# Revit family: J2 PET Felt Geo Panelsl
name_source: partatom
category: Generic Models
units: mm (PartAtom-declared; Revit-internal decimal feet)

## family parameters
Can host rebar = No
Cut with Voids When Loaded = No
Host = Face
Maintain Annotation Orientation = No
Part Type = Normal
Room Calculation Point = No
Round Connector Dimension = Use Diameter
Shared = No

## types (12) — shared parameters
Beveled Edges = Yes
Default Elevation = 0' - 0"
Felt color = <By Category>
Manufacturer = J2 Systems
Product Line = Geo Panel
Release Date = 2020
URL = https://www.j2systems.net

## per-type parameters (varying)
| type | Length | Thickness | Width |
| Geo Panel 1.5"x9"x9" | 0' - 9" | 0' - 1 1/2" | 0' - 9" |
| Geo Panel 1.5"x18"x18" | 1' - 6" | 0' - 1 1/2" | 1' - 6" |
| Geo Panel 1.5"x36"x36" | 3' - 0" | 0' - 1 1/2" | 3' - 0" |
| Geo Panel 1.5"x36"x18" | 3' - 0" | 0' - 1 1/2" | 1' - 6" |
| Geo Panel 1.5"x36"x9" | 3' - 0" | 0' - 1 1/2" | 0' - 9" |
| Geo Panel 1.5"x18"x9" | 1' - 6" | 0' - 1 1/2" | 0' - 9" |
| Geo Panel 2"x9"x9" | 0' - 9" | 0' - 2" | 0' - 9" |
| Geo Panel 2"x18"x18" | 1' - 6" | 0' - 2" | 1' - 6" |
| Geo Panel 2"x36"x36" | 3' - 0" | 0' - 2" | 3' - 0" |
| Geo Panel 2"x36"x18" | 3' - 0" | 0' - 2" | 1' - 6" |
| Geo Panel 2"x36"x9" | 3' - 0" | 0' - 2" | 0' - 9" |
| Geo Panel 2"x18"x9" | 1' - 6" | 0' - 2" | 0' - 9" |

## geometry (parser evidence)
native form markers: Sweep x3
no freeform markers — native parametric forms only
